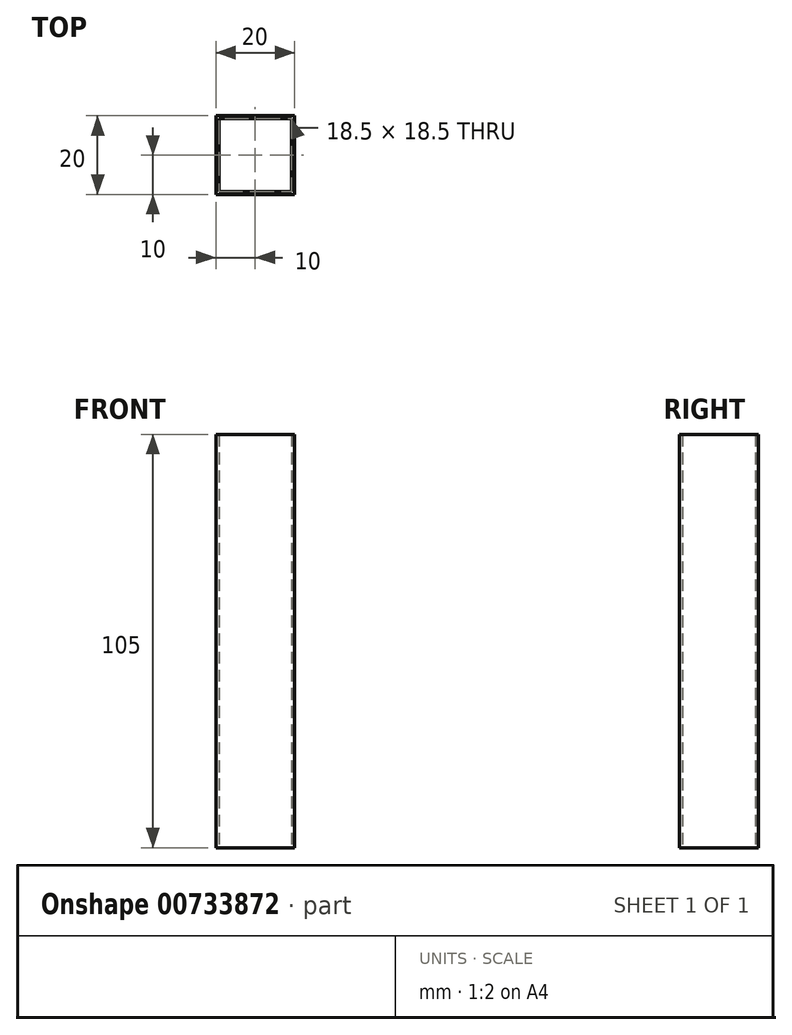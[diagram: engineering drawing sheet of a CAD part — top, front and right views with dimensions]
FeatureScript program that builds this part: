
annotation { "Feature Type Name" : "Feature", "Feature Type Description" : "" }
export const myFeature = defineFeature(function(context is Context, id is Id, definition is map)
    precondition{}
    {
        {
            var Q0;
            Q0=qCreatedBy(makeId("Top.planeOp"),FACE);
            var sketch = newSketch(context, id + "F0", { "sketchPlane" : qUnion([Q0])});
            skLineSegment(sketch, "E0.bottom", {"start": v(10, 10) * mm, "end": v(-10, 10) * mm});
            skLineSegment(sketch, "E0.top", {"start": v(10, -10) * mm, "end": v(-10, -10) * mm});
            skLineSegment(sketch, "E0.left", {"start": v(10, 10) * mm, "end": v(10, -10) * mm});
            skLineSegment(sketch, "E0.right", {"start": v(-10, 10) * mm, "end": v(-10, -10) * mm});
            skPoint(sketch, "E0.middle", {"position": v(0, 0) * mm});
            skLineSegment(sketch, "E1.bottom", {"start": v(9.25, 9.25) * mm, "end": v(-9.25, 9.25) * mm});
            skLineSegment(sketch, "E1.top", {"start": v(9.25, -9.25) * mm, "end": v(-9.25, -9.25) * mm});
            skLineSegment(sketch, "E1.left", {"start": v(9.25, 9.25) * mm, "end": v(9.25, -9.25) * mm});
            skLineSegment(sketch, "E1.right", {"start": v(-9.25, 9.25) * mm, "end": v(-9.25, -9.25) * mm});
            skSolve(sketch);
        }
        {
            var Q0;
            Q0=makeQuery(id+"F0.imprint","IMPRINT",FACE,{"disambiguationData":[TD([[makeQuery(id+"F0.imprint","IMPRINT",EDGE,{"derivedFrom":sQuery(id+"F0.wireOp",EDGE,"E0.bottom")}),1.0]])]});
            extrude(context, id + "F1", {"entities" : qUnion([Q0]), "depth" : (145 - 40) * mm, "offsetDistance" : 25 * mm});
        }
    });
